# Revit family: Fresh_f91
name_source: partatom
category: Plumbing Fixtures
units: mm (PartAtom-declared; Revit-internal decimal feet)

## family parameters
Always vertical = Yes
Cut with Voids When Loaded = No
Part Type = Normal
Room Calculation Point = No
Round Connector Dimension = Use Diameter
Shared = No
Work Plane-Based = No

## types (1)
- Fresh_f91
    Design Country = Slovenia
    Manufacturer Country = Slovenia
    Manufacturer Name = HERZ/Unitas
    Masterformat 2024 Code = 22 41 39
    Masterformat 2024 Description = Residential Faucets, Supplies, and Trim
    Material = Nickel chromium-plated
    Product Family = Fresh
    Product Group = Rosette and handle for concealed shower mixer
    Product Name = 12260 Fresh
    Product SKU = 12260
    Type = B91 : b91
    UNSPSC Code = 3018
    URL = http://www.herz-taps.com
    Uniclass 2015 Code = Pr_40_20_87
    Uniclass 2015 Name = Taps and water supply outlet fittings
    Uniformat II Code = D2010
    Uniformat II Description = Plumbing Fixtures
    Website 1 = www.unitas.rs
    Website 2 = www.herz.rs
    Website 3 = www.herz.eu

## geometry (parser evidence)
native form markers: Sweep x13
no freeform markers — native parametric forms only
